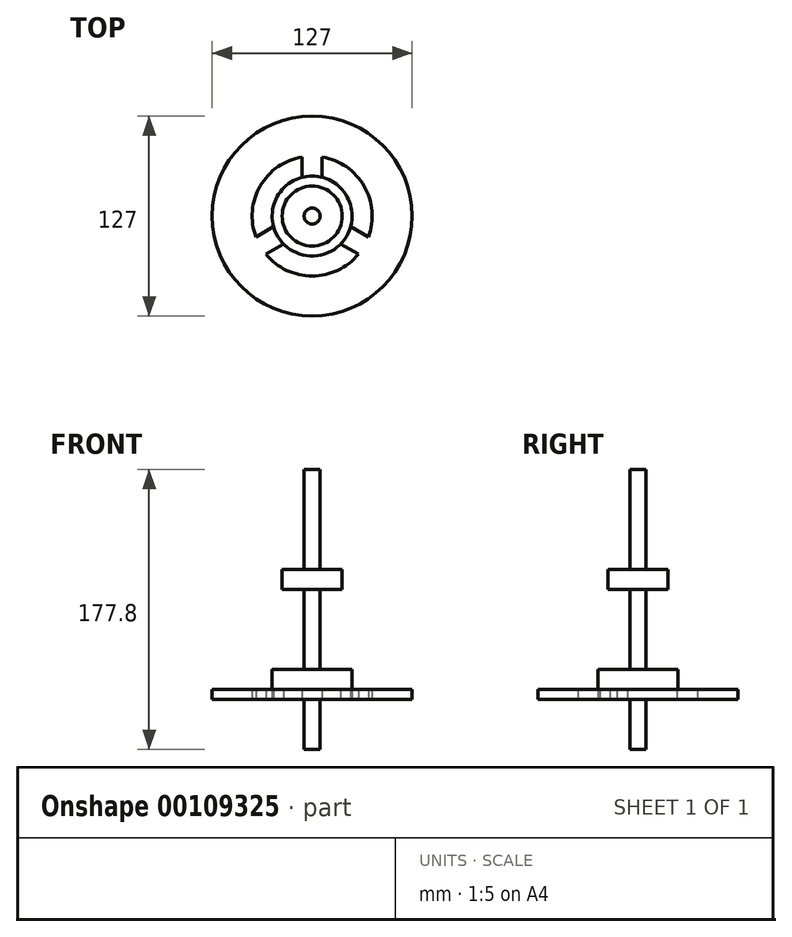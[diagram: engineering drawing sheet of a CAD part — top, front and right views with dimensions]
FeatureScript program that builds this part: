
annotation { "Feature Type Name" : "Feature", "Feature Type Description" : "" }
export const myFeature = defineFeature(function(context is Context, id is Id, definition is map)
    precondition{}
    {
        {
            var Q0;
            Q0=qCreatedBy(makeId("Top.planeOp"),FACE);
            var sketch = newSketch(context, id + "F0", { "sketchPlane" : qUnion([Q0])});
            skCircle(sketch, "E0", {"center": v(0, 0) * mm, "radius": 63.5 * mm});
            skCircle(sketch, "E1", {"center": v(0, 0) * mm, "radius": 38.1 * mm});
            skSolve(sketch);
        }
        {
            var Q0;
            Q0 = qSketchRegion(id + "F0", true);
            extrude(context, id + "F1", {"entities" : qUnion([Q0]), "depth" : 6.35 * mm});
        }
        {
            var Q0;
            Q0=qCreatedBy(makeId("Top.planeOp"),FACE);
            var sketch = newSketch(context, id + "F2", { "sketchPlane" : qUnion([Q0])});
            skCircle(sketch, "E2.0", {"center": v(0, 0) * mm, "radius": 50.8 * mm});
            skCircle(sketch, "E2.1", {"center": v(0, 0) * mm, "radius": 25.4 * mm});
            skLineSegment(sketch, "E3.1.0", {"start": v(-6.35, 50.4) * mm, "end": v(-6.35, 24.6) * mm});
            skLineSegment(sketch, "E3.1.1", {"start": v(6.35, 50.4) * mm, "end": v(6.35, 24.6) * mm});
            skLineSegment(sketch, "E4.1.0", {"start": v(-40.47, -30.7) * mm, "end": v(-18.12, -17.8) * mm});
            skLineSegment(sketch, "E4.1.1", {"start": v(-46.82, -19.7) * mm, "end": v(-24.47, -6.8) * mm});
            skLineSegment(sketch, "E4.2.0", {"start": v(46.82, -19.7) * mm, "end": v(24.47, -6.8) * mm});
            skLineSegment(sketch, "E4.2.1", {"start": v(40.47, -30.7) * mm, "end": v(18.12, -17.8) * mm});
            skSolve(sketch);
        }
        {
            var Q0;
            Q0=qCreatedBy(makeId("Top.planeOp"),FACE);
            var sketch = newSketch(context, id + "F3", { "sketchPlane" : qUnion([Q0])});
            skCircle(sketch, "E5", {"center": v(0, 0) * mm, "radius": 25.4 * mm});
            skSolve(sketch);
        }
        {
            var Q0;
            {var subQ0=sQuery(id+"F2.wireOp",EDGE,"E2.1");var subQ4=makeQuery(id+"F2.imprint","INTERSECT",VERTEX,{"derivedFrom":[subQ0,sQuery(id+"F2.wireOp",EDGE,"E3.1.0")]});Q0=makeQuery(id+"F2.imprint","IMPRINT",FACE,{"disambiguationData":[TD([[makeQuery(id+"F2.imprint","IMPRINT",EDGE,{"disambiguationData":[TD([[subQ4,1.0]])],"derivedFrom":subQ0}),1.0]])]});}
            var Q1;
            {var subQ0=sQuery(id+"F2.wireOp",EDGE,"E4.1.0");Q1=makeQuery(id+"F2.imprint","IMPRINT",FACE,{"disambiguationData":[TD([[makeQuery(id+"F2.imprint","IMPRINT",EDGE,{"derivedFrom":subQ0}),1.0]])]});}
            var Q2;
            {var subQ0=sQuery(id+"F2.wireOp",EDGE,"E3.1.0");Q2=makeQuery(id+"F2.imprint","IMPRINT",FACE,{"disambiguationData":[TD([[makeQuery(id+"F2.imprint","IMPRINT",EDGE,{"derivedFrom":subQ0}),1.0]])]});}
            var Q3;
            {var subQ0=sQuery(id+"F2.wireOp",EDGE,"E4.2.0");Q3=makeQuery(id+"F2.imprint","IMPRINT",FACE,{"disambiguationData":[TD([[makeQuery(id+"F2.imprint","IMPRINT",EDGE,{"derivedFrom":subQ0}),1.0]])]});}
            var Q4;
            Q4=makeQuery(id+"F1.opExtrude","CAP_FACE",FACE,{"disambiguationData":[OSD([sQuery(id+"F0.wireOp",EDGE,"E0"),sQuery(id+"F0.wireOp",EDGE,"E1")])],"isStart":false});
            extrude(context, id + "F4", {"entities" : qUnion([Q0, Q1, Q2, Q3]), "operationType" : NewBodyOperationType.ADD, "endBound" : BoundingType.UP_TO_SURFACE, "endBoundEntityFace" : qUnion([Q4]), "depth" : 25.4 * mm});
        }
        {
            var Q0;
            {var subQ0=sQuery(id+"F0.wireOp",EDGE,"E1");var subQ1=sQuery(id+"F0.wireOp",EDGE,"E0");Q0=makeQuery(id+"F4.boolean.opBoolean","MERGE",FACE,{"derivedFrom":[makeQuery(id+"F1.opExtrude","CAP_FACE",FACE,{"disambiguationData":[OSD([subQ1,subQ0])],"isStart":false}),makeQuery(id+"F4.opExtrude","CAP_FACE",FACE,{"disambiguationData":[OSD([subQ1,subQ0])],"isStart":false})]});}
            var sketch = newSketch(context, id + "F5", { "sketchPlane" : qUnion([Q0])});
            skCircle(sketch, "E6.0", {"center": v(0, 0) * mm, "radius": 25.4 * mm});
            skSolve(sketch);
        }
        {
            var Q0;
            Q0 = qSketchRegion(id + "F5", true);
            extrude(context, id + "F6", {"entities" : qUnion([Q0]), "operationType" : NewBodyOperationType.ADD, "depth" : 12.7 * mm});
        }
        {
            var Q0;
            Q0=makeQuery(id+"F6.opExtrude","CAP_FACE",FACE,{"disambiguationData":[OSD([sQuery(id+"F5.wireOp",EDGE,"E6.0")])],"isStart":false});
            var sketch = newSketch(context, id + "F7", { "sketchPlane" : qUnion([Q0])});
            skCircle(sketch, "E7", {"center": v(0, 0) * mm, "radius": 5.08 * mm});
            skSolve(sketch);
        }
        {
            var Q0;
            Q0 = qSketchRegion(id + "F7", true);
            var Q1;
            Q1=makeQuery(id+"F4.boolean.opBoolean","MERGE",FACE,{"derivedFrom":[makeQuery(id+"F1.opExtrude","CAP_FACE",FACE,{"disambiguationData":[OSD([sQuery(id+"F0.wireOp",EDGE,"E0"),sQuery(id+"F0.wireOp",EDGE,"E1")])],"isStart":true}),makeQuery(id+"F4.opExtrude","CAP_FACE",FACE,{"disambiguationData":[OSD([sQuery(id+"F2.wireOp",EDGE,"E2.0"),sQuery(id+"F2.wireOp",EDGE,"E2.1"),sQuery(id+"F2.wireOp",EDGE,"E3.1.0"),sQuery(id+"F2.wireOp",EDGE,"E3.1.1"),sQuery(id+"F2.wireOp",EDGE,"E4.1.0"),sQuery(id+"F2.wireOp",EDGE,"E4.1.1"),sQuery(id+"F2.wireOp",EDGE,"E4.2.0"),sQuery(id+"F2.wireOp",EDGE,"E4.2.1")])],"isStart":true})]});
            extrude(context, id + "F8", {"entities" : qUnion([Q0]), "operationType" : NewBodyOperationType.ADD, "oppositeDirection" : true, "endBoundEntityFace" : qUnion([Q1]), "depth" : 50.8 * mm});
        }
        {
            var Q0;
            Q0=makeQuery(id+"F6.opExtrude","CAP_FACE",FACE,{"disambiguationData":[OSD([sQuery(id+"F5.wireOp",EDGE,"E6.0")])],"isStart":false});
            var sketch = newSketch(context, id + "F9", { "sketchPlane" : qUnion([Q0])});
            skCircle(sketch, "E8.0", {"center": v(0, 0) * mm, "radius": 5.08 * mm});
            skCircle(sketch, "E8.2", {"center": v(0, 0) * mm, "radius": 25.4 * mm, "construction": true});
            skPoint(sketch, "E8.3", {"position": v(0, 0) * mm});
            skSolve(sketch);
        }
        {
            var Q0;
            Q0 = qSketchRegion(id + "F9", true);
            extrude(context, id + "F10", {"entities" : qUnion([Q0]), "operationType" : NewBodyOperationType.ADD, "depth" : 127 * mm});
        }
        {
            var Q0;
            Q0=qCreatedBy(makeId("Front.planeOp"),FACE);
            var sketch = newSketch(context, id + "F11", { "sketchPlane" : qUnion([Q0])});
            skLineSegment(sketch, "E9", {"start": v(0, 0) * mm, "end": v(0, 69.85) * mm, "construction": true});
            skSolve(sketch);
        }
        {
            var Q0;
            Q0=qCreatedBy(makeId("Top.planeOp"),FACE);
            var Q1;
            Q1=sQuery(id+"F11.wireOp",VERTEX,"E9.end");
            cPlane(context, id + "F12", {"entities" : qUnion([Q0, Q1]), "cplaneType" : CPlaneType.PLANE_POINT, "offset" : 25.4 * mm, "width" : 152.4 * mm, "height" : 152.4 * mm});
        }
        {
            var Q0;
            Q0=qCreatedBy(id+"F12.planeOp",FACE);
            var sketch = newSketch(context, id + "F13", { "sketchPlane" : qUnion([Q0])});
            skCircle(sketch, "E10", {"center": v(0, 0) * mm, "radius": 19.05 * mm});
            skSolve(sketch);
        }
        {
            var Q0;
            Q0 = qSketchRegion(id + "F13", true);
            extrude(context, id + "F14", {"entities" : qUnion([Q0]), "operationType" : NewBodyOperationType.ADD, "depth" : 12.7 * mm});
        }
    });
